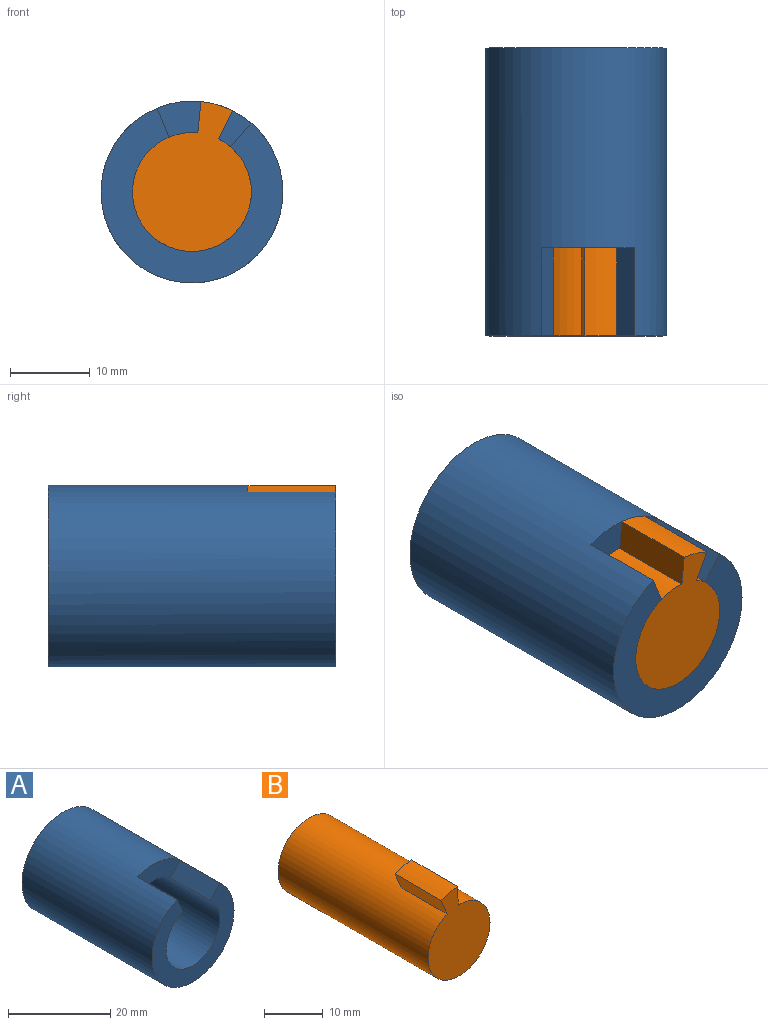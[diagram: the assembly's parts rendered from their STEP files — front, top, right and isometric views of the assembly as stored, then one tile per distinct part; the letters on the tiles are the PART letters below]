
ASSEMBLY  parts=2 mates=1
PART A: 7 faces, bbox 22.7x36x22.7 mm
  f0: plane 11.74x5.71mm, normal (0,-1,0), area 40.6mm2, adj f1,f2,f4,f5
  f1: cylinder r=7.44mm len=36mm, axis (0,1,0), area 1591.9mm2, adj f0,f3,f4,f5,f6
  f2: cylinder r=11.36mm len=36mm, axis (0,1,0), area 2432.5mm2, adj f0,f3,f4,f5,f6
  f3: plane 22.72x22.72mm, normal (0,1,0), area 231.9mm2, adj f1,f2
  f4: plane 11x2.98mm, normal (-0.76,0,0.65), area 43.2mm2, adj f0,f1,f2,f6
  f5: plane 11x3.63mm, normal (0.92,0,0.38), area 43.2mm2, adj f0,f1,f2,f6
  f6: plane 22.72x21.86mm, normal (0,-1,0), area 191.3mm2, adj f1,f2,f4,f5
PART B: 7 faces, bbox 14.9x36x18.8 mm
  f0: plane 18.79x14.87mm, normal (0,-1,0), area 187.2mm2, adj f1,f3,f4,f5
  f1: plane 11x3.93mm, normal (1,0,0.03), area 43.2mm2, adj f0,f2,f3,f4
  f2: plane 4.49x4.14mm, normal (0,1,0), area 13.5mm2, adj f1,f3,f4,f5
  f3: cylinder r=11.36mm len=11mm, axis (0,1,0), area 45.6mm2, adj f0,f1,f2,f5
  f4: cylinder r=7.44mm len=36mm, axis (0,1,0), area 1652.1mm2, adj f0,f1,f2,f5,f6
  f5: plane 11x3.63mm, normal (-0.92,0,-0.38), area 43.2mm2, adj f0,f2,f3,f4
  f6: plane 14.87x14.87mm, normal (0,1,0), area 173.7mm2, adj f4
PLACE A at identity fixed
PLACE B rot(axis=(0,1,0),28.2deg) t=(0,0,0)mm
MATE revolute B.f4 <-> A.f2  axis (0,1,0) through (0,0,0)mm
